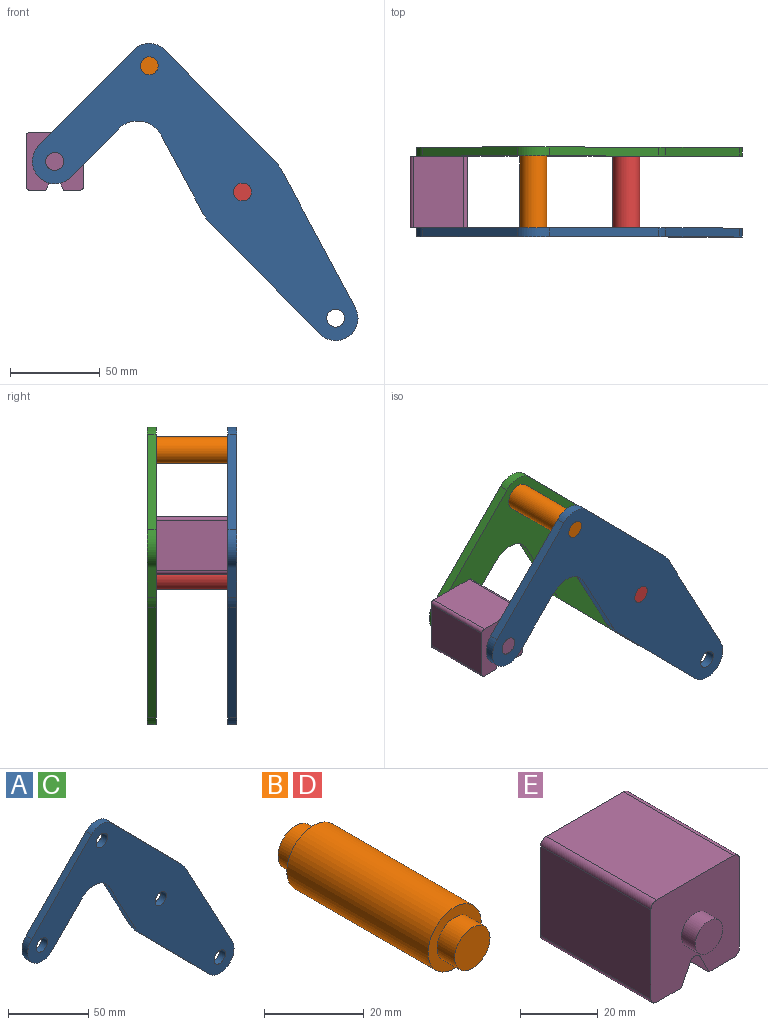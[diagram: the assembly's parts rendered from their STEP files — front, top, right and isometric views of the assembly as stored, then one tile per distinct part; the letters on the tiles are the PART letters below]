
ASSEMBLY  parts=5 mates=3
PART A: 18 faces, bbox 181.7x5x165.8 mm
  f0: plane 43.49x23.35mm, normal (-0.88,0,-0.47), area 246.8mm2, adj f1,f14,f16,f17
  f1: cylinder r=25mm len=5.75mm, axis (0,1,0), area 35.8mm2, adj f0,f2,f16,f17
  f2: plane 61.6x60.87mm, normal (-0.71,0,-0.7), area 433mm2, adj f1,f3,f16,f17
  f3: cylinder r=12.5mm len=21.39mm, axis (0,1,0), area 178.4mm2, adj f2,f4,f16,f17
  f4: plane 76.3x40.96mm, normal (0.88,0,0.47), area 433mm2, adj f3,f5,f16,f17
  f5: cylinder r=25mm len=5.75mm, axis (0,1,0), area 35.8mm2, adj f4,f6,f16,f17
  f6: plane 61.6x60.87mm, normal (0.71,0,0.7), area 433mm2, adj f5,f7,f16,f17
  f7: cylinder r=12.5mm len=17.78mm, axis (0,1,0), area 98.9mm2, adj f6,f8,f16,f17
  f8: plane 53.35x52.71mm, normal (-0.71,0,0.7), area 375mm2, adj f7,f9,f16,f17
  f9: cylinder r=12.5mm len=21.39mm, axis (0,1,0), area 196.3mm2, adj f8,f10,f16,f17
  f10: plane 26.86x26.54mm, normal (0.71,0,-0.7), area 188.8mm2, adj f9,f14,f16,f17
  f11: cylinder r=5mm len=10mm, axis (0,1,0), area 157.1mm2, adj f16,f17
  f12: cylinder r=5mm len=10mm, axis (0,1,0), area 157.1mm2, adj f16,f17
  f13: cylinder r=5mm len=10mm, axis (0,1,0), area 157.1mm2, adj f16,f17
  f14: cylinder r=15mm len=23.89mm, axis (0,1,0), area 140.2mm2, adj f0,f10,f16,f17
  f15: cylinder r=5mm len=10mm, axis (0,1,0), area 157.1mm2, adj f16,f17
  f16: plane 181.66x165.78mm, normal (0,-1,0), area 8710.1mm2, adj f0,f1,f2,f3,f4,f5,f6,f7
  f17: plane 181.66x165.78mm, normal (0,1,0), area 8710.1mm2, adj f0,f1,f2,f3,f4,f5,f6,f7
PART B: 7 faces, bbox 15x50x15 mm
  f0: cylinder r=7.5mm len=40mm, axis (0,-1,0), area 1885mm2, adj f2,f5
  f1: cylinder r=5mm len=10mm, axis (0,1,0), area 157.1mm2, adj f2,f3
  f2: plane 15x15mm, normal (0,-1,0), area 98.2mm2, adj f0,f1
  f3: plane 10x10mm, normal (0,-1,0), area 78.5mm2, adj f1
  f4: cylinder r=5mm len=10mm, axis (0,-1,0), area 157.1mm2, adj f5,f6
  f5: plane 15x15mm, normal (0,1,0), area 98.2mm2, adj f0,f4
  f6: plane 10x10mm, normal (0,1,0), area 78.5mm2, adj f4
PART C: same geometry as A
PART D: same geometry as B
PART E: 18 faces, bbox 32.1x50x32.1 mm
  f0: plane 40x28.08mm, normal (1,0,0), area 1123.1mm2, adj f4,f10,f13,f14
  f1: plane 40x9.04mm, normal (0,0,-1), area 361.6mm2, adj f2,f4,f10,f14
  f2: plane 40x6.42mm, normal (-0.89,0,-0.45), area 287.2mm2, adj f1,f4,f10,f15
  f3: plane 40x6.42mm, normal (0.89,0,-0.45), area 287.2mm2, adj f4,f5,f10,f15
  f4: plane 32.08x32.08mm, normal (0,-1,0), area 900.6mm2, adj f0,f1,f2,f3,f5,f6,f7,f9
  f5: plane 40x9.04mm, normal (0,0,-1), area 361.6mm2, adj f3,f4,f10,f16
  f6: plane 40x28.08mm, normal (0,0,1), area 1123.1mm2, adj f4,f10,f13,f17
  f7: plane 40x28.08mm, normal (-1,0,0), area 1123.1mm2, adj f4,f10,f16,f17
  f8: plane 10x10mm, normal (0,-1,0), area 78.5mm2, adj f9
  f9: cylinder r=5mm len=10mm, axis (0,1,0), area 157.1mm2, adj f4,f8
  f10: plane 32.08x32.08mm, normal (0,1,0), area 900.6mm2, adj f0,f1,f2,f3,f5,f6,f7,f12
  f11: plane 10x10mm, normal (0,1,0), area 78.5mm2, adj f12
  f12: cylinder r=5mm len=10mm, axis (0,-1,0), area 157.1mm2, adj f10,f11
  f13: cylinder r=2mm len=40mm, axis (0,1,0), area 125.7mm2, adj f0,f4,f6,f10
  f14: cylinder r=2mm len=40mm, axis (0,-1,0), area 125.7mm2, adj f0,f1,f4,f10
  f15: cylinder r=2mm len=40mm, axis (0,1,0), area 177.1mm2, adj f2,f3,f4,f10
  f16: cylinder r=2mm len=40mm, axis (0,1,0), area 125.7mm2, adj f4,f5,f7,f10
  f17: cylinder r=2mm len=40mm, axis (0,-1,0), area 125.7mm2, adj f4,f6,f7,f10
PLACE A t=(0,-20,0)mm fixed
PLACE B t=(0,-20,0)mm
PLACE C t=(0,25,0)mm
PLACE D t=(51.98,-20,-70.39)mm
PLACE E t=(0,-20,0)mm
MATE fastened C.f7 <-> B.f0  axis (0,-1,0) through (-51.98,20,70.39)mm
MATE revolute E.f9 <-> A.f9  axis (0,-1,0) through (-104.69,-20,17.04)mm
MATE fastened A.f1 <-> D.f0  axis (0,1,0) through (0,-20,0)mm
